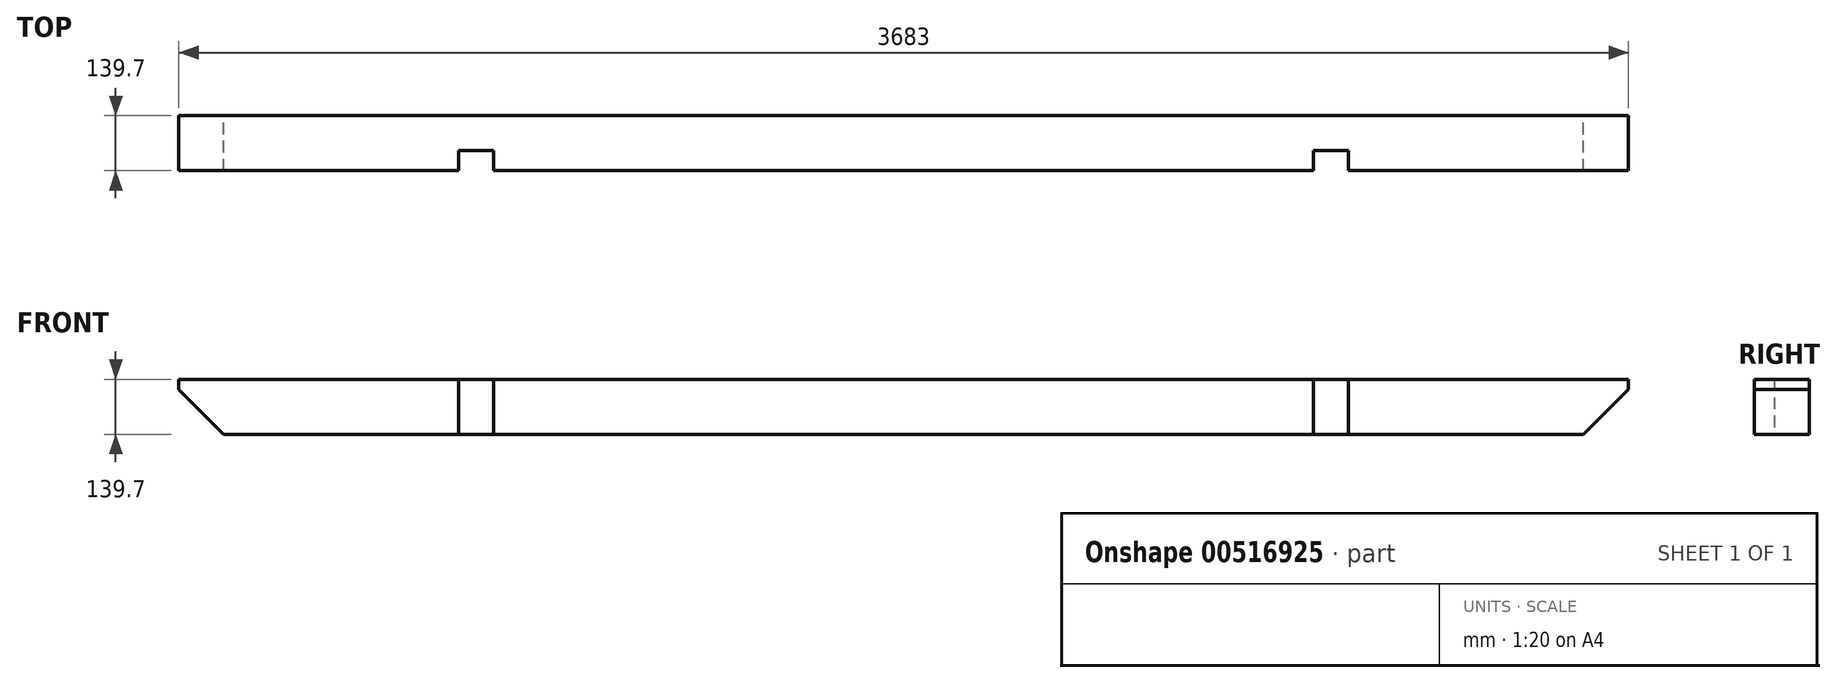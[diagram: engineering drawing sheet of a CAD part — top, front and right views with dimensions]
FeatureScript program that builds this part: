
annotation { "Feature Type Name" : "Feature", "Feature Type Description" : "" }
export const myFeature = defineFeature(function(context is Context, id is Id, definition is map)
    precondition{}
    {
        {
            var Q0;
            Q0=qCreatedBy(makeId("Front.planeOp"),FACE);
            var sketch = newSketch(context, id + "F0", { "sketchPlane" : qUnion([Q0])});
            skLineSegment(sketch, "E0", {"start": v(0, 0) * mm, "end": v(0, -25.4) * mm});
            skLineSegment(sketch, "E1", {"start": v(0, -25.4) * mm, "end": v(114.3, -139.7) * mm});
            skLineSegment(sketch, "E2", {"start": v(114.3, -139.7) * mm, "end": v(3568.7, -139.7) * mm});
            skLineSegment(sketch, "E3", {"start": v(3568.7, -139.7) * mm, "end": v(3683, -25.4) * mm});
            skLineSegment(sketch, "E4", {"start": v(3683, -25.4) * mm, "end": v(3683, 0) * mm});
            skLineSegment(sketch, "E5", {"start": v(3683, 0) * mm, "end": v(0, 0) * mm});
            skSolve(sketch);
        }
        {
            var Q0;
            Q0=makeQuery(id+"F0.imprint","IMPRINT",FACE,{"disambiguationData":[TD([[makeQuery(id+"F0.imprint","IMPRINT",EDGE,{"derivedFrom":sQuery(id+"F0.wireOp",EDGE,"E0")}),1.0]])]});
            extrude(context, id + "F1", {"entities" : qUnion([Q0]), "depth" : 139.7 * mm, "offsetDistance" : 25.4 * mm});
        }
        {
            var Q0;
            Q0=makeQuery(id+"F1.opExtrude","CAP_FACE",FACE,{"disambiguationData":[OSD([sQuery(id+"F0.wireOp",EDGE,"E0"),sQuery(id+"F0.wireOp",EDGE,"E1"),sQuery(id+"F0.wireOp",EDGE,"E2"),sQuery(id+"F0.wireOp",EDGE,"E3"),sQuery(id+"F0.wireOp",EDGE,"E4"),sQuery(id+"F0.wireOp",EDGE,"E5")])],"isStart":false});
            var sketch = newSketch(context, id + "F2", { "sketchPlane" : qUnion([Q0])});
            skLineSegment(sketch, "E6.0.0", {"start": v(3683, -25.4) * mm, "end": v(3683, 0) * mm});
            skLineSegment(sketch, "E6.0.2", {"start": v(0, 0) * mm, "end": v(0, -25.4) * mm});
            skLineSegment(sketch, "E6.0.3", {"start": v(0, -25.4) * mm, "end": v(114.3, -139.7) * mm});
            skLineSegment(sketch, "E6.0.5", {"start": v(3568.7, -139.7) * mm, "end": v(3683, -25.4) * mm});
            skLineSegment(sketch, "E7.bottom", {"start": v(711.2, 0) * mm, "end": v(800.1, 0) * mm});
            skLineSegment(sketch, "E7.top", {"start": v(711.2, -139.7) * mm, "end": v(800.1, -139.7) * mm});
            skLineSegment(sketch, "E7.left", {"start": v(711.2, 0) * mm, "end": v(711.2, -139.7) * mm});
            skLineSegment(sketch, "E7.right", {"start": v(800.1, 0) * mm, "end": v(800.1, -139.7) * mm});
            skLineSegment(sketch, "E8.bottom", {"start": v(2882.9, 0) * mm, "end": v(2971.8, 0) * mm});
            skLineSegment(sketch, "E8.top", {"start": v(2882.9, -139.7) * mm, "end": v(2971.8, -139.7) * mm});
            skLineSegment(sketch, "E8.left", {"start": v(2882.9, 0) * mm, "end": v(2882.9, -139.7) * mm});
            skLineSegment(sketch, "E8.right", {"start": v(2971.8, 0) * mm, "end": v(2971.8, -139.7) * mm});
            skSolve(sketch);
        }
        {
            var Q0;
            Q0 = qSketchRegion(id + "F2", true);
            extrude(context, id + "F3", {"entities" : qUnion([Q0]), "operationType" : NewBodyOperationType.REMOVE, "oppositeDirection" : true, "depth" : 50.8 * mm, "offsetDistance" : 25.4 * mm});
        }
    });
